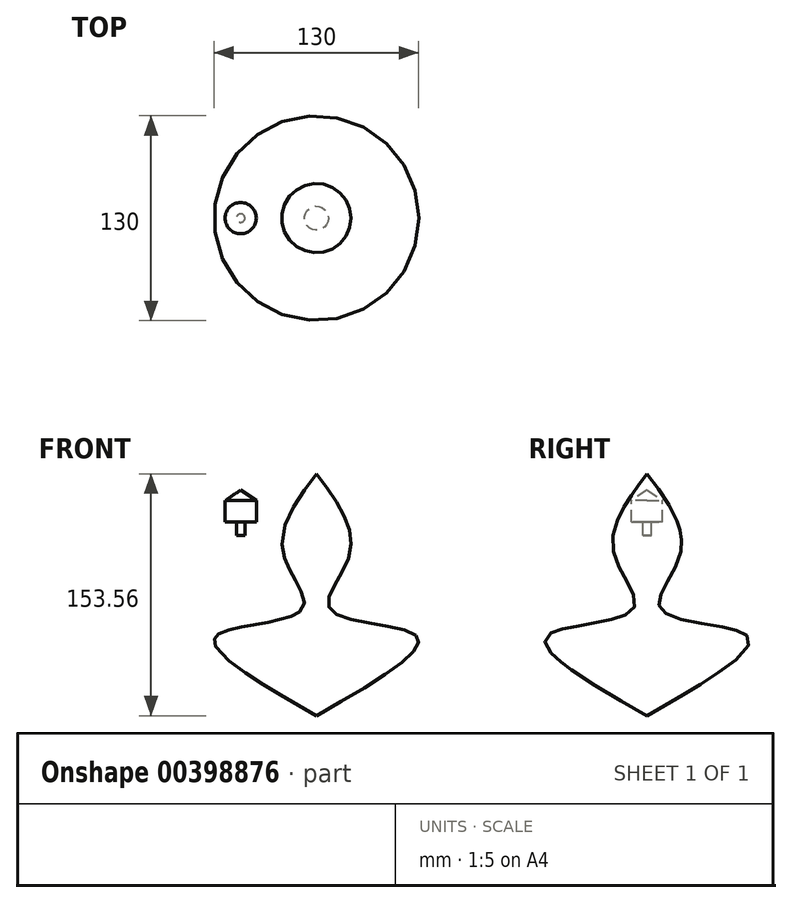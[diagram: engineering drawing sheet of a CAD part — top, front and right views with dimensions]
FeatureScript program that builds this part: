
annotation { "Feature Type Name" : "Feature", "Feature Type Description" : "" }
export const myFeature = defineFeature(function(context is Context, id is Id, definition is map)
    precondition{}
    {
        {
            var Q0;
            Q0=qCreatedBy(makeId("Front.planeOp"),FACE);
            var sketch = newSketch(context, id + "F0", { "sketchPlane" : qUnion([Q0])});
            skLineSegment(sketch, "E0", {"start": v(0, 76.32) * mm, "end": v(0, -77.24) * mm});
            skFitSpline(sketch, "E1", {"points": [v(0, 76.32) * mm, v(21.2, 26) * mm, v(9.03, -9.96) * mm, v(63.6, -26.55) * mm, v(0, -77.24) * mm], "startDerivative": vector(154.42, -204.4) * mm, "endDerivative": vector(-363.98, -208.08) * mm});
            skSolve(sketch);
        }
        {
            var Q0;
            Q0=makeQuery(id+"F0.imprint","IMPRINT",FACE,{"disambiguationData":[TD([[makeQuery(id+"F0.imprint","IMPRINT",EDGE,{"derivedFrom":sQuery(id+"F0.wireOp",EDGE,"E0")}),1.0]])]});
            var Q1;
            Q1=sQuery(id+"F0.wireOp",EDGE,"E0");
            revolve(context, id + "F1", {"entities" : qUnion([Q0]), "axis" : qUnion([Q1]), "revolveType" : RevolveType.FULL});
        }
        {
            var Q0;
            Q0=qCreatedBy(makeId("Front.planeOp"),FACE);
            var sketch = newSketch(context, id + "F2", { "sketchPlane" : qUnion([Q0])});
            skLineSegment(sketch, "E2", {"start": v(-48.09, 66.16) * mm, "end": v(-48.09, 37.33) * mm});
            skLineSegment(sketch, "E3", {"start": v(-48.09, 37.33) * mm, "end": v(-45.42, 37.33) * mm});
            skLineSegment(sketch, "E4", {"start": v(-45.42, 37.33) * mm, "end": v(-45.42, 45.86) * mm});
            skLineSegment(sketch, "E5", {"start": v(-45.42, 45.86) * mm, "end": v(-38.17, 45.86) * mm});
            skLineSegment(sketch, "E6", {"start": v(-38.17, 45.86) * mm, "end": v(-38.17, 59.33) * mm});
            skLineSegment(sketch, "E7", {"start": v(-38.17, 59.33) * mm, "end": v(-48.09, 66.16) * mm});
            skSolve(sketch);
        }
        {
            var Q0;
            Q0=makeQuery(id+"F2.imprint","IMPRINT",FACE,{"disambiguationData":[TD([[makeQuery(id+"F2.imprint","IMPRINT",EDGE,{"derivedFrom":sQuery(id+"F2.wireOp",EDGE,"E2")}),1.0]])]});
            var Q1;
            Q1=sQuery(id+"F2.wireOp",EDGE,"E2");
            revolve(context, id + "F3", {"entities" : qUnion([Q0]), "axis" : qUnion([Q1]), "revolveType" : RevolveType.FULL});
        }
    });
